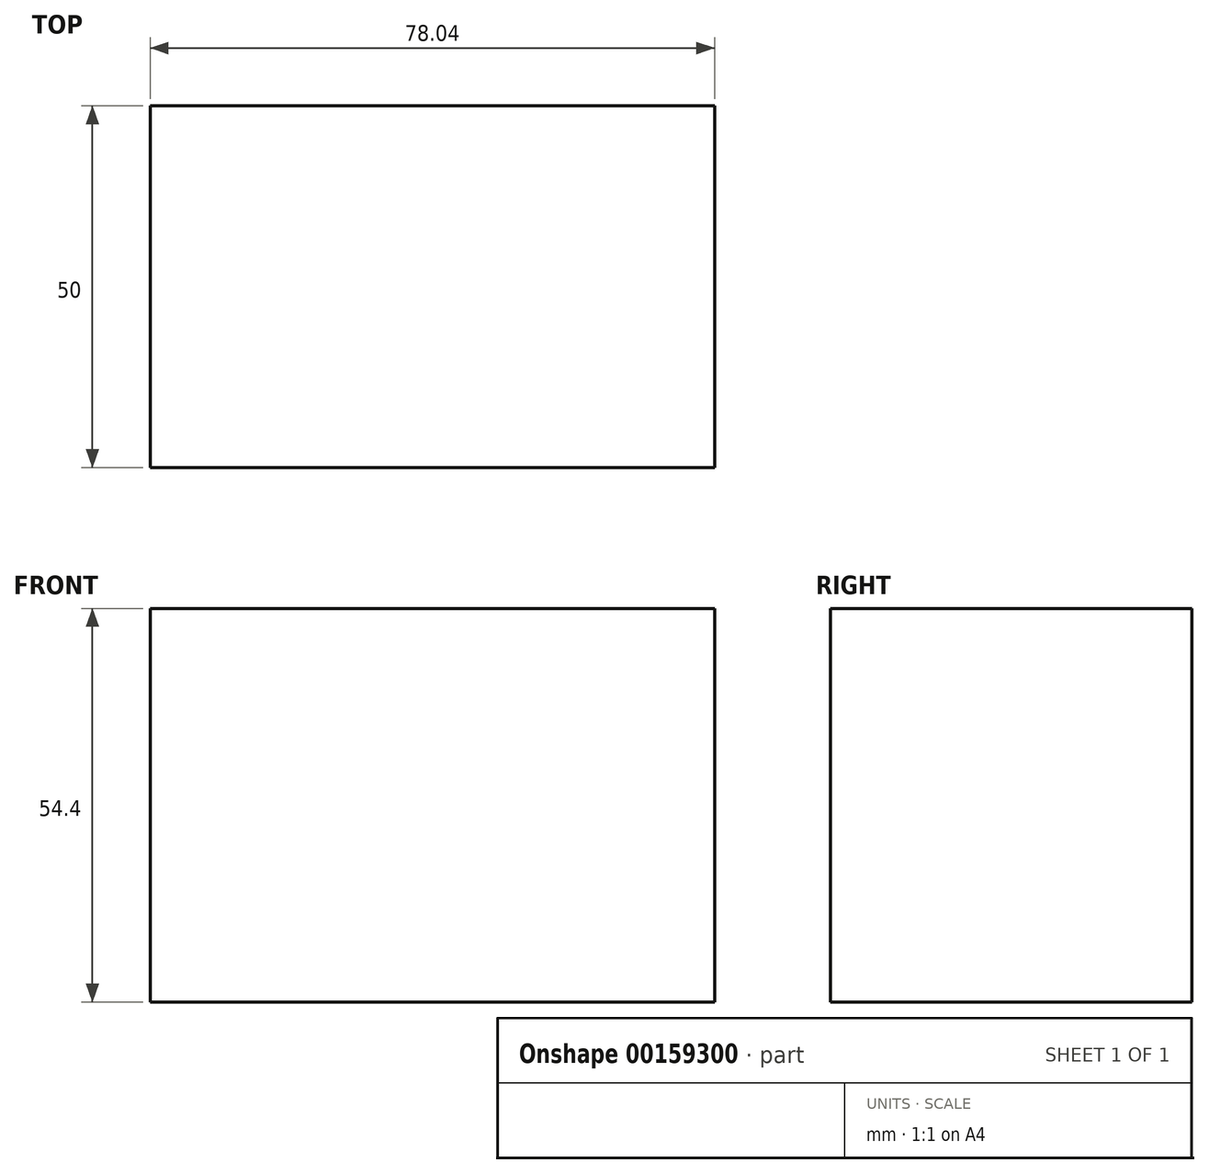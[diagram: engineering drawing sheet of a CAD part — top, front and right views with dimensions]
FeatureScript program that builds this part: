
annotation { "Feature Type Name" : "Feature", "Feature Type Description" : "" }
export const myFeature = defineFeature(function(context is Context, id is Id, definition is map)
    precondition{}
    {
        {
            var Q0;
            Q0=qCreatedBy(makeId("Front.planeOp"),FACE);
            var sketch = newSketch(context, id + "F0", { "sketchPlane" : qUnion([Q0])});
            skLineSegment(sketch, "E0.bottom", {"start": v(39.02, -27.2) * mm, "end": v(-39.02, -27.2) * mm});
            skLineSegment(sketch, "E0.top", {"start": v(39.02, 27.2) * mm, "end": v(-39.02, 27.2) * mm});
            skLineSegment(sketch, "E0.left", {"start": v(39.02, -27.2) * mm, "end": v(39.02, 27.2) * mm});
            skLineSegment(sketch, "E0.right", {"start": v(-39.02, -27.2) * mm, "end": v(-39.02, 27.2) * mm});
            skPoint(sketch, "E0.middle", {"position": v(0, 0) * mm});
            skSolve(sketch);
        }
        {
            var Q0;
            Q0=makeQuery(id+"F0.imprint","IMPRINT",FACE,{"disambiguationData":[TD([[makeQuery(id+"F0.imprint","IMPRINT",EDGE,{"derivedFrom":sQuery(id+"F0.wireOp",EDGE,"E0.bottom")}),-1.0]])]});
            extrude(context, id + "F1", {"entities" : qUnion([Q0]), "depth" : 25 * mm});
        }
        {
            var Q0;
            Q0=makeQuery(id+"F1.opExtrude","CAP_FACE",FACE,{"disambiguationData":[OSD([sQuery(id+"F0.wireOp",EDGE,"E0.bottom"),sQuery(id+"F0.wireOp",EDGE,"E0.top"),sQuery(id+"F0.wireOp",EDGE,"E0.left"),sQuery(id+"F0.wireOp",EDGE,"E0.right")])],"isStart":true});
            extrude(context, id + "F2", {"entities" : qUnion([Q0]), "operationType" : NewBodyOperationType.ADD, "depth" : 25 * mm});
        }
    });
